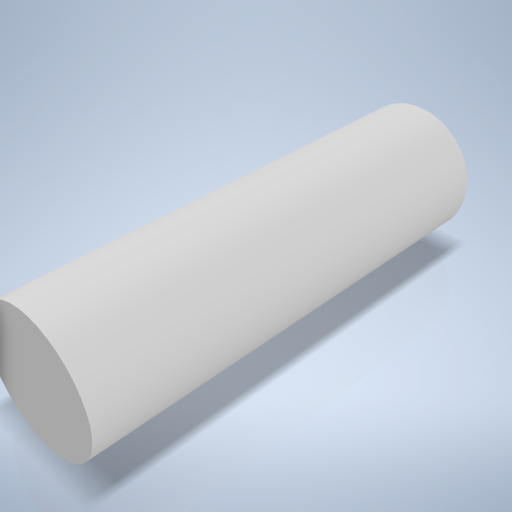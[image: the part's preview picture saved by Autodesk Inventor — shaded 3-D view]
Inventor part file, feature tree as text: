
AUTODESK INVENTOR PART (.ipt)
format: ipt  version: 2024.2 (Build 282272000, 272)  size: 213,504 bytes
history: native  units: mm
features: extrude x1, sketch x1
ambient origin geometry x8: Origin, YZ Plane, XZ Plane, XY Plane, X Axis, Y Axis, Z Axis, Center Point
bodies: Volumenkörper1 (feature_tree)
feature tree (2):
  extrude  "Extrusion1"  Depth=40.0mm TaperAngle=0.0deg
  sketch  "Skizze1"  dims[d0=12.0mm d1=40.0mm d2=0.0mm]
